# Revit family: Gohome_UtilityStool_R21
name_source: partatom
category: Furniture
units: mm (PartAtom-declared; Revit-internal decimal feet)

## family parameters
Always vertical = Yes
Cut with Voids When Loaded = No
OmniClass Number = 23.40.20.00
OmniClass Title = General Furniture and Specialties
Room Calculation Point = No
Shared = No
Work Plane-Based = No

## types (2) — shared parameters
Frame Material = <By Category>
Manufacturer = gohome
Model = Utility Counter And Bar Stool
Seat Material = <By Category>
URL = www.gohome.com.au
zero-valued in all types: Default Elevation

## per-type parameters (varying)
| type | Bar Stool | Depth | Height | LegHeightCalc | Width |
| Bar Stool | Yes | 420 mm  [stored 1.37795 ft] | 650 mm  [stored 2.13255 ft] | 600 mm | 400 mm  [stored 1.31234 ft] |
| Counter Stool | No | 460 mm  [stored 1.50919 ft] | 750 mm  [stored 2.46063 ft] | 700 mm  [stored 2.29659 ft] | 407 mm  [stored 1.3353 ft] |

type visibility flags (boolean, named after types; folded from table):
- Bar Stool: Yes: (none)
- Counter Stool: Yes: Counter Stool

note: [stored X ft] marks values corroborated as IEEE doubles in the binary element streams (Revit-internal decimal feet)

## geometry (parser evidence)
native form markers: Sweep x3
no freeform markers — native parametric forms only
